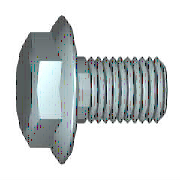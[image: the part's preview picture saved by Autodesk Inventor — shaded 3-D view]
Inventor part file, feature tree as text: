
AUTODESK INVENTOR PART (.ipt)
format: ipt  version: 2013 (Build 170138000, 138)  size: 219,136 bytes
history: native  units: mm (DEFAULTED — no unit token found)
features: sketch x3, extrude x1, chamfer x1, plane x1
ambient origin geometry x7: Origin, YZ Plane, XZ Plane, X Axis, Y Axis, Z Axis, Center Point
bodies: Solid1 (feature_tree), Body (feature_tree)
feature tree (6):
  extrude  "Head"  Depth=12.7mm
  chamfer  "Chamfer1"  Distance=6.35mm
  plane  "Work Plane1"
  sketch  "Sketch1"  dims[d0=1.016mm d1=12.7mm]
  sketch  "Sketch2"  dims[d2=10.795mm]
  sketch  "Sketch3"  dims[d3=14.224mm d4=6.35mm d5=3.2004mm d12=90.0deg d6=7.112mm d7=0.0mm d8=30.0deg d21=90.0deg d10=10.795mm d11=0.0mm d13=0.779082mm d14=0.779081mm d15=6.35mm d16=6.35mm d17=0.0001mm d18=1.27mm d19=4.363323mm d20=0.0mm d22=9.525mm d23=9.525mm d39=45.0deg d40=0.0mm d41=0.0mm]
